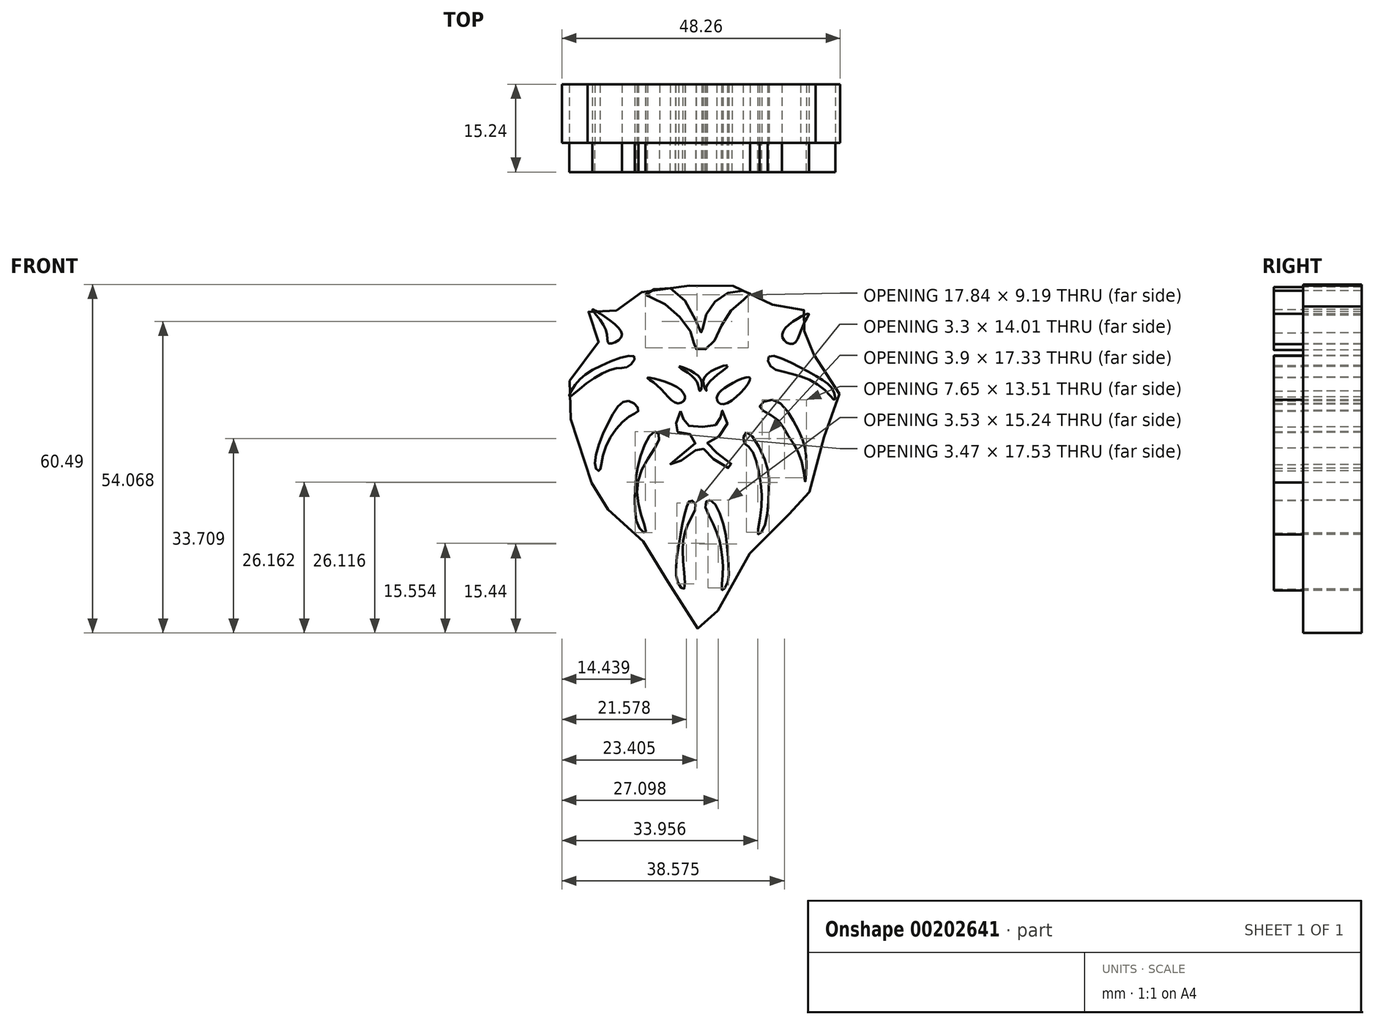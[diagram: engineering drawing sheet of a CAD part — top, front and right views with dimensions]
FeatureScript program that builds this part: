
annotation { "Feature Type Name" : "Feature", "Feature Type Description" : "" }
export const myFeature = defineFeature(function(context is Context, id is Id, definition is map)
    precondition{}
    {
        {
            var Q0;
            Q0=qCreatedBy(makeId("Front.planeOp"),FACE);
            var sketch = newSketch(context, id + "F0", { "sketchPlane" : qUnion([Q0])});
            skFitSpline(sketch, "E0", {"points": [v(-10.59, 12.32) * mm, v(-18.16, 11.73) * mm, v(-21.6, 7.99) * mm, v(-23.87, 8.19) * mm, v(-28.1, 8.48) * mm, v(-27.41, 6.8) * mm, v(-26.04, 3.86) * mm, v(-29.18, -1.95) * mm, v(-32.63, -6.57) * mm, v(-29.68, -13.95) * mm, v(-26.63, -25.17) * mm, v(-25.74, -25.96) * mm, v(-20.92, -29.2) * mm, v(-16.69, -35.1) * mm, v(-12.55, -41.93) * mm, v(-8.16, -47.91) * mm, v(-6.82, -46.58) * mm, v(-1.34, -36.13) * mm, v(5.53, -28.17) * mm, v(9.93, -25.12) * mm, v(10.25, -23.33) * mm, v(13.18, -13.14) * mm, v(15.58, -7) * mm, v(12.3, -1.86) * mm, v(9.36, 2.71) * mm, v(8.72, 2.93) * mm, v(11.36, 8.43) * mm, v(9.22, 8.08) * mm, v(5.65, 7.36) * mm, v(1.71, 11.15) * mm, v(-4.65, 12.3) * mm, v(-10.59, 12.32) * mm]});
            skFitSpline(sketch, "E1", {"points": [v(-22.38, 3.36) * mm, v(-23.87, 5.93) * mm, v(-27.41, 8.19) * mm, v(-25.02, 4.64) * mm, v(-24.52, 2.29) * mm, v(-22.38, 3.36) * mm]});
            skFitSpline(sketch, "E2", {"points": [v(5.57, 3.36) * mm, v(7.29, 6) * mm, v(10.15, 7.43) * mm, v(9.22, 5.57) * mm, v(7.43, 2.21) * mm, v(5.57, 3.36) * mm]});
            skFitSpline(sketch, "E3", {"points": [v(-8.58, 0) * mm, v(-15.3, 5.07) * mm, v(-16.59, 3.36) * mm, v(-21.95, -5.08) * mm, v(-21.1, -5.8) * mm, v(-15.37, -12.15) * mm, v(-14.3, -14.73) * mm, v(-14.87, -19.52) * mm, v(-13.3, -20.88) * mm, v(-8.65, -24.88) * mm, v(-6.58, -22.8) * mm, v(-1.93, -19.73) * mm, v(-2.72, -18.16) * mm, v(1, -8.3) * mm, v(5.57, -5.94) * mm, v(3.43, -2.58) * mm, v(-1.65, 5) * mm, v(-4.72, 2.36) * mm, v(-8.58, 0) * mm]});
            skFitSpline(sketch, "E4", {"points": [v(-11.3, -7.3) * mm, v(-13.08, -5.08) * mm, v(-17.8, -3.65) * mm, v(-16.01, -5.08) * mm, v(-12.73, -8.08) * mm, v(-11.3, -7.3) * mm]});
            skFitSpline(sketch, "E5", {"points": [v(0, -3.72) * mm, v(-3.93, -5.08) * mm, v(-5.8, -7.3) * mm, v(-4.43, -8.22) * mm, v(0, -3.72) * mm]});
            skFitSpline(sketch, "E6", {"points": [v(-12.08, -9.44) * mm, v(-12.94, -12.73) * mm, v(-11.94, -13.08) * mm, v(-9.37, -14.66) * mm, v(-13.87, -18.52) * mm, v(-12.85, -18.52) * mm, v(-8.58, -15.8) * mm, v(-7.65, -16.59) * mm, v(-3.36, -19.38) * mm, v(-3.36, -18.52) * mm, v(-7.44, -15.01) * mm, v(-4.15, -12.73) * mm, v(-4.93, -9.3) * mm, v(-5.22, -11.08) * mm, v(-6.58, -12.01) * mm, v(-10.59, -12.01) * mm, v(-11.58, -10.94) * mm, v(-12.08, -9.44) * mm]});
            skFitSpline(sketch, "E7", {"points": [v(-12.37, -1.72) * mm, v(-8.65, -3.8) * mm, v(-8.72, -5.94) * mm, v(-9.44, -4.08) * mm, v(-12.37, -1.72) * mm]});
            skFitSpline(sketch, "E8", {"points": [v(-3.93, -1.58) * mm, v(-8, -3.72) * mm, v(-7.58, -5.94) * mm, v(-7.58, -5.08) * mm, v(-3.93, -1.58) * mm]});
            skFitSpline(sketch, "E9", {"points": [v(-18.16, 10.72) * mm, v(-13.37, 11.73) * mm, v(-8.44, 4.14) * mm, v(-8, 6.15) * mm, v(-3.86, 11.08) * mm, v(0, 11) * mm, v(-3.36, 8) * mm, v(-7.22, 1.57) * mm, v(-9.58, 1.5) * mm, v(-10, 3.5) * mm, v(-16.01, 9.86) * mm, v(-18.16, 10.72) * mm]});
            skFitSpline(sketch, "E10", {"points": [v(-30.38, -4.86) * mm, v(-25.8, -1.5) * mm, v(-20.09, 0) * mm, v(-21.1, -1.65) * mm, v(-23.45, -2.08) * mm, v(-28.95, -5.08) * mm, v(-31.38, -6.94) * mm, v(-30.38, -4.86) * mm]});
            skFitSpline(sketch, "E11", {"points": [v(-21.1, -7.65) * mm, v(-24.38, -10.94) * mm, v(-26.88, -19.09) * mm, v(-26.17, -19.8) * mm, v(-25.45, -16.66) * mm, v(-21.1, -10.44) * mm, v(-19.37, -9.22) * mm, v(-21.1, -7.65) * mm]});
            skFitSpline(sketch, "E12", {"points": [v(-16.59, -13.01) * mm, v(-19.09, -17.44) * mm, v(-20.02, -24.3) * mm, v(-19.23, -29.74) * mm, v(-18.16, -30.53) * mm, v(-19.02, -27.1) * mm, v(-18.95, -19.88) * mm, v(-15.73, -13.87) * mm, v(-16.59, -13.01) * mm]});
            skFitSpline(sketch, "E13", {"points": [v(-12.55, -39.23) * mm, v(-12.55, -33.7) * mm, v(-11.2, -26.54) * mm, v(-10.3, -24.94) * mm, v(-9.44, -25.74) * mm, v(-10.87, -29.2) * mm, v(-11.67, -34.98) * mm, v(-11.51, -40.28) * mm, v(-12.55, -39.23) * mm]});
            skFitSpline(sketch, "E14", {"points": [v(-6.93, -24.88) * mm, v(-4.67, -28.96) * mm, v(-3.79, -35.71) * mm, v(-3.95, -39.25) * mm, v(-4.83, -40.53) * mm, v(-4.75, -37.64) * mm, v(-5, -33.62) * mm, v(-6.28, -29.28) * mm, v(-7.81, -25.5) * mm, v(-6.93, -24.88) * mm]});
            skFitSpline(sketch, "E15", {"points": [v(3.23, 0) * mm, v(7.43, -1.19) * mm, v(12.57, -4.08) * mm, v(14.4, -5.8) * mm, v(14.7, -7.5) * mm, v(12.95, -5.8) * mm, v(7.43, -3.01) * mm, v(3.53, -1.64) * mm, v(3.23, 0) * mm]});
            skFitSpline(sketch, "E16", {"points": [v(3.84, -7.48) * mm, v(7.43, -11.05) * mm, v(9.46, -15.68) * mm, v(9.76, -19.4) * mm, v(9.54, -21.82) * mm, v(8.93, -18.16) * mm, v(6.65, -13.78) * mm, v(4.22, -10.51) * mm, v(1.64, -8.69) * mm, v(3.84, -7.48) * mm]});
            skFitSpline(sketch, "E17", {"points": [v(-0.64, -13.16) * mm, v(2.62, -18.16) * mm, v(3.23, -23.33) * mm, v(2.32, -29.85) * mm, v(1.4, -30.83) * mm, v(1.86, -27.12) * mm, v(1.56, -20.21) * mm, v(0, -15.89) * mm, v(-1.17, -14.75) * mm, v(-0.64, -13.16) * mm]});
            skSolve(sketch);
        }
        {
            var Q0;
            Q0 = qSketchRegion(id + "F0", true);
            var Q1;
            Q1=makeQuery(id+"F0.imprint","IMPRINT",FACE,{"disambiguationData":[TD([[makeQuery(id+"F0.imprint","IMPRINT",EDGE,{"derivedFrom":sQuery(id+"F0.wireOp",EDGE,"E3")}),1.0]])]});
            extrude(context, id + "F1", {"entities" : qUnion([Q0, Q1]), "oppositeDirection" : true, "depth" : 10.16 * mm});
        }
        {
            var Q0;
            Q0=makeQuery(id+"F0.imprint","IMPRINT",FACE,{"disambiguationData":[TD([[makeQuery(id+"F0.imprint","IMPRINT",EDGE,{"derivedFrom":sQuery(id+"F0.wireOp",EDGE,"E9")}),-1.0]])]});
            var Q1;
            Q1=makeQuery(id+"F0.imprint","IMPRINT",FACE,{"disambiguationData":[TD([[makeQuery(id+"F0.imprint","IMPRINT",EDGE,{"derivedFrom":sQuery(id+"F0.wireOp",EDGE,"E1")}),1.0]])]});
            var Q2;
            Q2=makeQuery(id+"F0.imprint","IMPRINT",FACE,{"disambiguationData":[TD([[makeQuery(id+"F0.imprint","IMPRINT",EDGE,{"derivedFrom":sQuery(id+"F0.wireOp",EDGE,"E10")}),-1.0]])]});
            var Q3;
            Q3=makeQuery(id+"F0.imprint","IMPRINT",FACE,{"disambiguationData":[TD([[makeQuery(id+"F0.imprint","IMPRINT",EDGE,{"derivedFrom":sQuery(id+"F0.wireOp",EDGE,"E11")}),1.0]])]});
            var Q4;
            Q4=makeQuery(id+"F0.imprint","IMPRINT",FACE,{"disambiguationData":[TD([[makeQuery(id+"F0.imprint","IMPRINT",EDGE,{"derivedFrom":sQuery(id+"F0.wireOp",EDGE,"E12")}),1.0]])]});
            var Q5;
            Q5=makeQuery(id+"F0.imprint","IMPRINT",FACE,{"disambiguationData":[TD([[makeQuery(id+"F0.imprint","IMPRINT",EDGE,{"derivedFrom":sQuery(id+"F0.wireOp",EDGE,"E13")}),-1.0]])]});
            var Q6;
            Q6=makeQuery(id+"F0.imprint","IMPRINT",FACE,{"disambiguationData":[TD([[makeQuery(id+"F0.imprint","IMPRINT",EDGE,{"derivedFrom":sQuery(id+"F0.wireOp",EDGE,"E14")}),-1.0]])]});
            var Q7;
            Q7=makeQuery(id+"F0.imprint","IMPRINT",FACE,{"disambiguationData":[TD([[makeQuery(id+"F0.imprint","IMPRINT",EDGE,{"derivedFrom":sQuery(id+"F0.wireOp",EDGE,"E17")}),-1.0]])]});
            var Q8;
            Q8=makeQuery(id+"F0.imprint","IMPRINT",FACE,{"disambiguationData":[TD([[makeQuery(id+"F0.imprint","IMPRINT",EDGE,{"derivedFrom":sQuery(id+"F0.wireOp",EDGE,"E16")}),-1.0]])]});
            var Q9;
            Q9=makeQuery(id+"F0.imprint","IMPRINT",FACE,{"disambiguationData":[TD([[makeQuery(id+"F0.imprint","IMPRINT",EDGE,{"derivedFrom":sQuery(id+"F0.wireOp",EDGE,"E15")}),-1.0]])]});
            var Q10;
            Q10=makeQuery(id+"F0.imprint","IMPRINT",FACE,{"disambiguationData":[TD([[makeQuery(id+"F0.imprint","IMPRINT",EDGE,{"derivedFrom":sQuery(id+"F0.wireOp",EDGE,"E2")}),-1.0]])]});
            var Q11;
            Q11=makeQuery(id+"F0.imprint","IMPRINT",FACE,{"disambiguationData":[TD([[makeQuery(id+"F0.imprint","IMPRINT",EDGE,{"derivedFrom":sQuery(id+"F0.wireOp",EDGE,"E8")}),1.0]])]});
            var Q12;
            Q12=makeQuery(id+"F0.imprint","IMPRINT",FACE,{"disambiguationData":[TD([[makeQuery(id+"F0.imprint","IMPRINT",EDGE,{"derivedFrom":sQuery(id+"F0.wireOp",EDGE,"E7")}),-1.0]])]});
            var Q13;
            Q13=makeQuery(id+"F0.imprint","IMPRINT",FACE,{"disambiguationData":[TD([[makeQuery(id+"F0.imprint","IMPRINT",EDGE,{"derivedFrom":sQuery(id+"F0.wireOp",EDGE,"E4")}),1.0]])]});
            var Q14;
            Q14=makeQuery(id+"F0.imprint","IMPRINT",FACE,{"disambiguationData":[TD([[makeQuery(id+"F0.imprint","IMPRINT",EDGE,{"derivedFrom":sQuery(id+"F0.wireOp",EDGE,"E5")}),1.0]])]});
            var Q15;
            Q15=makeQuery(id+"F0.imprint","IMPRINT",FACE,{"disambiguationData":[TD([[makeQuery(id+"F0.imprint","IMPRINT",EDGE,{"derivedFrom":sQuery(id+"F0.wireOp",EDGE,"E6")}),1.0]])]});
            extrude(context, id + "F2", {"entities" : qUnion([Q0, Q1, Q2, Q3, Q4, Q5, Q6, Q7, Q8, Q9, Q10, Q11, Q12, Q13, Q14, Q15]), "depth" : 5.08 * mm});
        }
    });
